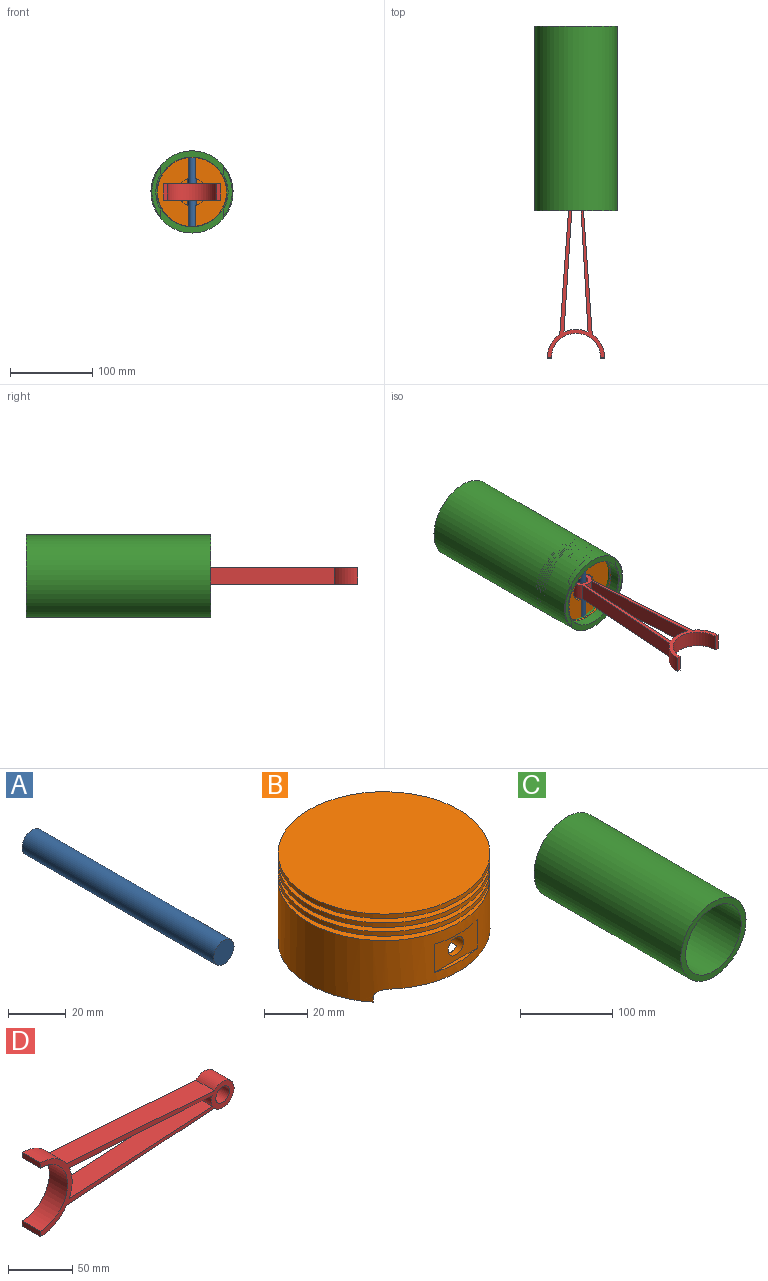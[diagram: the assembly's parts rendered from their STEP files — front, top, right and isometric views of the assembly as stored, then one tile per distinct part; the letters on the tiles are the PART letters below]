
ASSEMBLY  parts=4 mates=3
PART A: 3 faces, bbox 10x94x10 mm
  f0: plane 10x10mm, normal (0,-1,0), area 78.5mm2, adj f1
  f1: cylinder r=5mm len=94mm, axis (0,1,0), area 2953.1mm2, adj f0,f2
  f2: plane 10x10mm, normal (0,1,0), area 78.5mm2, adj f1
PART B: 45 faces, bbox 98x98x50 mm
  f0: plane 87.67x40.2mm, normal (0,0,-1), area 2381.3mm2, adj f21,f23,f43,f44
  f1: cylinder r=49mm len=98mm, axis (0,0,1), area 8604.6mm2, adj f2,f4,f5,f27,f28,f29,f30,f31
  f2: plane 61.87x11mm, normal (0,0,-1), area 285mm2, adj f1,f3,f31,f32
  f3: cylinder r=44mm len=88mm, axis (0,0,1), area 1981.1mm2, adj f2,f4,f26,f27,f28,f29,f30,f31
  f4: plane 61.87x11mm, normal (0,0,-1), area 285mm2, adj f1,f3,f27,f34
  f5: plane 98x98mm, normal (0,0,1), area 1460.8mm2, adj f1,f6
  f6: cylinder r=44mm len=88mm, axis (0,0,1), area 691.2mm2, adj f5,f7
  f7: plane 98x98mm, normal (0,0,-1), area 1460.8mm2, adj f6,f8
  f8: cylinder r=49mm len=98mm, axis (0,0,1), area 769.7mm2, adj f7,f9
  f9: plane 98x98mm, normal (0,0,1), area 1460.8mm2, adj f8,f10
  f10: cylinder r=44mm len=88mm, axis (0,0,1), area 691.2mm2, adj f9,f11
  f11: plane 98x98mm, normal (0,0,-1), area 1460.8mm2, adj f10,f12
  f12: cylinder r=49mm len=98mm, axis (0,0,1), area 769.7mm2, adj f11,f13
  f13: plane 98x98mm, normal (0,0,1), area 1460.8mm2, adj f12,f14
  f14: cylinder r=44mm len=88mm, axis (0,0,1), area 691.2mm2, adj f13,f15
  f15: plane 98x98mm, normal (0,0,-1), area 1460.8mm2, adj f14,f16
  f16: cylinder r=49mm len=98mm, axis (0,0,1), area 769.7mm2, adj f15,f17
  f17: plane 98x98mm, normal (0,0,1), area 7543mm2, adj f16
  f18: plane 52x52mm, normal (0,0,-1), area 2123.7mm2, adj f19
  f19: cylinder r=26mm len=52mm, axis (0,0,1), area 2450.4mm2, adj f18,f20
  f20: plane 52x52mm, normal (0,0,1), area 1215.8mm2, adj f19,f21
  f21: cylinder r=17mm len=34mm, axis (0,0,1), area 1461.8mm2, adj f0,f20,f22,f43,f44
  f22: plane 87.67x40.2mm, normal (0,0,-1), area 2381.3mm2, adj f21,f23,f43,f44
  f23: cylinder r=44mm len=88mm, axis (0,0,1), area 949.1mm2, adj f0,f22,f24,f43,f44
  f24: plane 88x88mm, normal (0,0,1), area 540.4mm2, adj f23,f25
  f25: cylinder r=42mm len=84mm, axis (0,0,1), area 527.8mm2, adj f24,f26
  f26: plane 88x88mm, normal (0,0,-1), area 540.4mm2, adj f3,f25
  f27: plane 8.75x2.5mm, normal (1,0,0), area 21.9mm2, adj f1,f3,f4,f28
  f28: cylinder r=5mm len=14.04mm, axis (0,1,0), area 63.4mm2, adj f1,f3,f27,f29
  f29: plane 66x19.9mm, normal (0,0,-1), area 367.1mm2, adj f1,f3,f28,f30
  f30: cylinder r=5mm len=14.04mm, axis (0,1,0), area 63.4mm2, adj f1,f3,f29,f31
  f31: plane 8.75x2.5mm, normal (-1,0,0), area 21.9mm2, adj f1,f2,f3,f30
  f32: plane 8.75x2.5mm, normal (-1,0,0), area 21.9mm2, adj f1,f2,f3,f33
  f33: cylinder r=5mm len=14.04mm, axis (0,1,0), area 63.4mm2, adj f1,f3,f32,f35
  f34: plane 8.75x2.5mm, normal (1,0,0), area 21.9mm2, adj f1,f3,f4,f36
  f35: plane 66x19.9mm, normal (0,0,-1), area 367.1mm2, adj f1,f3,f33,f36
  f36: cylinder r=5mm len=14.04mm, axis (0,1,0), area 63.4mm2, adj f1,f3,f34,f35
  f37: plane 27.71x2mm, normal (0,0,-1), area 37.1mm2, adj f1,f39
  f38: plane 27.71x2mm, normal (0,0,1), area 37.1mm2, adj f1,f39
  f39: plane 27.71x16mm, normal (0,-1,0), area 364.9mm2, adj f1,f37,f38,f44
  f40: plane 27.71x2mm, normal (0,0,-1), area 37.1mm2, adj f1,f42
  f41: plane 27.71x2mm, normal (0,0,1), area 37.1mm2, adj f1,f42
  f42: plane 27.71x16mm, normal (0,1,0), area 364.9mm2, adj f1,f40,f41,f43
  f43: cylinder r=5mm len=30.75mm, axis (0,-1,0), area 720.5mm2, adj f0,f21,f22,f23,f42
  f44: cylinder r=5mm len=30.75mm, axis (0,-1,0), area 720.5mm2, adj f0,f21,f22,f23,f39
PART C: 5 faces, bbox 100x225x100 mm
  f0: cylinder r=42.5mm len=200mm, axis (0,1,0), area 53407.1mm2, adj f2,f3
  f1: cylinder r=50mm len=225mm, axis (0,1,0), area 70685.8mm2, adj f2,f4
  f2: plane 100x100mm, normal (0,-1,0), area 2179.5mm2, adj f0,f1
  f3: plane 85x85mm, normal (0,-1,0), area 5674.5mm2, adj f0
  f4: plane 100x100mm, normal (0,1,0), area 7854mm2, adj f1
PART D: 15 faces, bbox 212.5x20x70 mm
  f0: cylinder r=12.5mm len=20mm, axis (0,1,0), area 210.6mm2, adj f1,f12,f13,f14
  f1: plane 157.05x20mm, normal (-0.06,0,1), area 3146.2mm2, adj f0,f2,f13,f14
  f2: cylinder r=35mm len=29.27mm, axis (0,1,0), area 603.9mm2, adj f1,f12,f13,f14
  f3: cylinder r=35mm len=28.85mm, axis (0,1,0), area 678.4mm2, adj f4,f10,f13,f14
  f4: plane 20x5mm, normal (-1,0,0), area 100mm2, adj f3,f5,f13,f14
  f5: cylinder r=30mm len=60mm, axis (0,1,0), area 1885mm2, adj f4,f6,f13,f14
  f6: plane 20x5mm, normal (-1,0,0), area 100mm2, adj f5,f7,f13,f14
  f7: cylinder r=35mm len=28.85mm, axis (0,1,0), area 678.4mm2, adj f6,f8,f13,f14
  f8: plane 161.85x20mm, normal (0.07,0,-1), area 3245mm2, adj f7,f9,f13,f14
  f9: cylinder r=12.5mm len=25mm, axis (0,1,0), area 1205mm2, adj f8,f10,f13,f14
  f10: plane 161.85x20mm, normal (0.07,0,1), area 3245mm2, adj f3,f9,f13,f14
  f11: cylinder r=7.5mm len=20mm, axis (0,1,0), area 942.5mm2, adj f13,f14
  f12: plane 156.57x20mm, normal (-0.06,0,-1), area 3137.9mm2, adj f0,f2,f13,f14
  f13: plane 212.5x70mm, normal (0,-1,0), area 2155.9mm2, adj f0,f1,f2,f3,f4,f5,f6,f7
  f14: plane 212.5x70mm, normal (0,1,0), area 2155.9mm2, adj f0,f1,f2,f3,f4,f5,f6,f7
PLACE A rot(axis=(-1,0,0),90deg) t=(0,-171.25,0)mm
PLACE B rot(axis=(-1,0,0),90deg) t=(0,-171.25,0)mm
PLACE C at identity fixed
PLACE D rot(axis=(-0.58,-0.58,0.58),120deg) t=(0,-179.25,-10)mm
MATE slider C.f0 <-> B.f1  axis (0,-1,0) through (0,0,0)mm
MATE fastened B.f43 <-> A.f1  axis (0,0,1) through (0,-179.25,47)mm
MATE fastened D.f9 <-> A.f1  axis (0,0,-1) through (0,-179.25,0)mm
